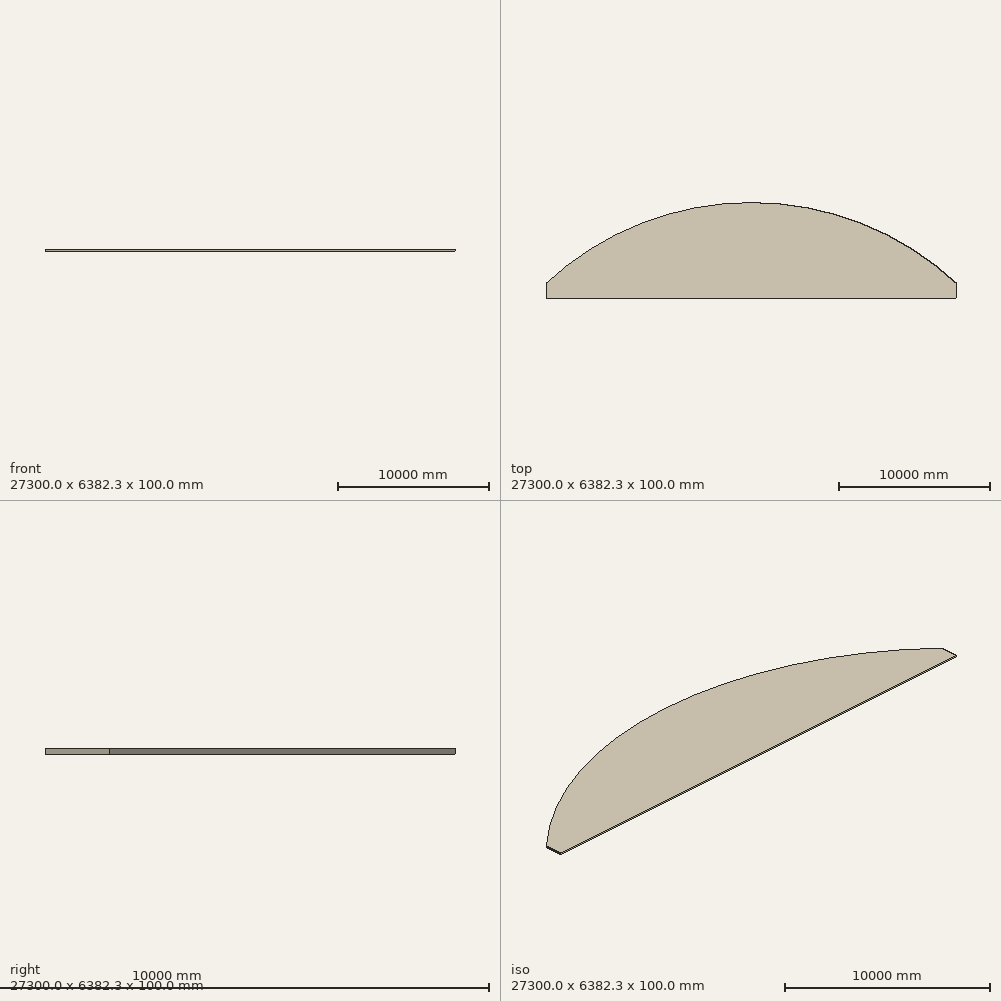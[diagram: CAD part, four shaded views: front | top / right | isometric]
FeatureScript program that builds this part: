
annotation { "Feature Type Name" : "Feature", "Feature Type Description" : "" }
export const myFeature = defineFeature(function(context is Context, id is Id, definition is map)
    precondition{}
    {
        {
            var Q0;
            Q0=qCreatedBy(makeId("Top.planeOp"),FACE);
            var sketch = newSketch(context, id + "F0", { "sketchPlane" : qUnion([Q0])});
            skLineSegment(sketch, "E0.top", {"start": v(-13604.53, 3213.46) * mm, "end": v(13695.47, 3213.46) * mm});
            skLineSegment(sketch, "E0.left", {"start": v(-13604.53, 4213.46) * mm, "end": v(-13604.53, 3213.46) * mm});
            skLineSegment(sketch, "E0.right", {"start": v(13695.47, 4213.46) * mm, "end": v(13695.47, 3213.46) * mm});
            skArc(sketch, "E1", {"start": v(13695.47, 4213.46) * mm, "mid": v(45.47, 9595.75) * mm, "end": v(-13604.53, 4213.46) * mm});
            skSolve(sketch);
        }
        {
            var Q0;
            Q0=qSketchRegion(id+"F0",true);
            extrude(context, id + "F1", {"entities" : qUnion([Q0]), "depth" : 100 * mm});
        }
    });
